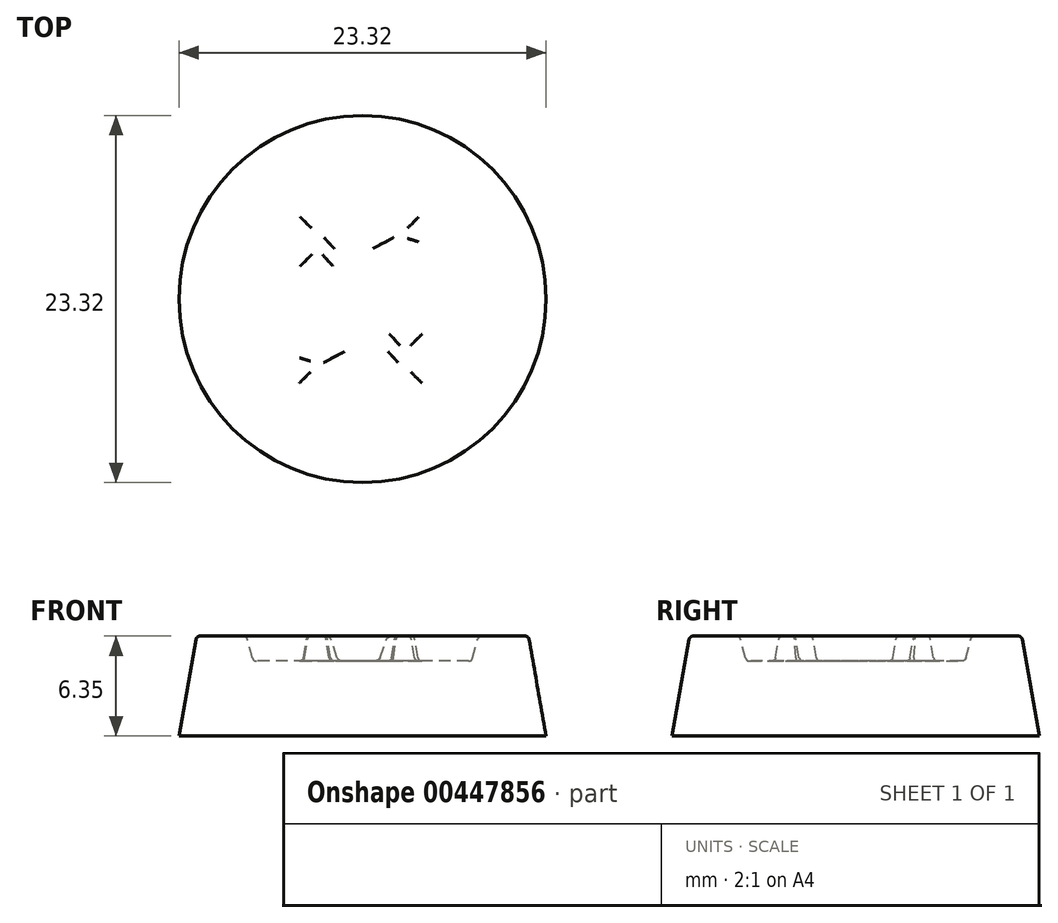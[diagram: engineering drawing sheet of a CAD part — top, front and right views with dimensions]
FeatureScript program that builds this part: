
annotation { "Feature Type Name" : "Feature", "Feature Type Description" : "" }
export const myFeature = defineFeature(function(context is Context, id is Id, definition is map)
    precondition{}
    {
        {
            var Q0;
            Q0=qCreatedBy(makeId("Top.planeOp"),FACE);
            var sketch = newSketch(context, id + "F0", { "sketchPlane" : qUnion([Q0])});
            skCircle(sketch, "E0", {"center": v(0, 0) * mm, "radius": 10.54 * mm});
            skSolve(sketch);
        }
        {
            var Q0;
            Q0=makeQuery(id+"F0.imprint","IMPRINT",FACE,{"disambiguationData":[TD([[makeQuery(id+"F0.imprint","IMPRINT",EDGE,{"derivedFrom":sQuery(id+"F0.wireOp",EDGE,"E0")}),1.0]])]});
            extrude(context, id + "F1", {"entities" : qUnion([Q0]), "oppositeDirection" : true, "depth" : 6.35 * mm, "hasDraft" : true, "draftAngle" : 10 * degree});
        }
        {
            var Q0;
            Q0=makeQuery(id+"F1.opExtrude","CAP_FACE",FACE,{"disambiguationData":[OSD([sQuery(id+"F0.wireOp",EDGE,"E0")])],"isStart":true});
            var sketch = newSketch(context, id + "F2", { "sketchPlane" : qUnion([Q0])});
            skCircle(sketch, "E1.0", {"center": v(0, 0) * mm, "radius": 7.37 * mm});
            skSolve(sketch);
        }
        {
            var Q0;
            Q0=makeQuery(id+"F2.imprint","IMPRINT",FACE,{"disambiguationData":[TD([[makeQuery(id+"F2.imprint","IMPRINT",EDGE,{"derivedFrom":sQuery(id+"F2.wireOp",EDGE,"E1.0")}),1.0]])]});
            extrude(context, id + "F3", {"entities" : qUnion([Q0]), "operationType" : NewBodyOperationType.REMOVE, "oppositeDirection" : true, "depth" : 1.59 * mm, "hasDraft" : true, "draftAngle" : 15 * degree, "draftPullDirection" : true});
        }
        {
            var Q0;
            Q0=makeQuery(id+"F1.opExtrude","CAP_FACE",FACE,{"disambiguationData":[OSD([sQuery(id+"F0.wireOp",EDGE,"E0")])],"isStart":true});
            var sketch = newSketch(context, id + "F4", { "sketchPlane" : qUnion([Q0])});
            skText(sketch, "E2", { "text": "Z", "fontName": "RobotoSlab-Regular.ttf"});
            skCircle(sketch, "E3.0", {"center": v(0, 0) * mm, "radius": 6.35 * mm, "construction": true});
            const initialGuessF4  = {"E2": [-0.00412, -0.00484, 1, 0, 0.00967]};
            skSetInitialGuess(sketch, initialGuessF4);
            skSolve(sketch);
        }
        {
            var Q0;
            Q0=makeQuery(id+"F4.imprint","IMPRINT",FACE,{"disambiguationData":[TD([[makeQuery(id+"F4.imprint","IMPRINT",EDGE,{"derivedFrom":sQuery(id+"F4.wireOp",EDGE,"E2.sketch_text.stroke-0")}),-1.0]])]});
            var Q1;
            Q1=makeQuery(id+"F3.boolean.opBoolean","COPY",FACE,{"derivedFrom":makeQuery(id+"F3.opExtrude","CAP_FACE",FACE,{"disambiguationData":[OSD([sQuery(id+"F2.wireOp",EDGE,"E1.0")])],"isStart":false})});
            extrude(context, id + "F5", {"entities" : qUnion([Q0]), "operationType" : NewBodyOperationType.ADD, "endBound" : BoundingType.UP_TO_SURFACE, "oppositeDirection" : true, "endBoundEntityFace" : qUnion([Q1]), "depth" : 25.4 * mm, "hasDraft" : true, "draftAngle" : 10 * degree});
        }
        {
            var Q0;
            Q0=makeQuery(id+"F5.opExtrude","CAP_FACE",FACE,{"disambiguationData":[OSD([sQuery(id+"F4.wireOp",EDGE,"E2.sketch_text.stroke-0"),sQuery(id+"F4.wireOp",EDGE,"E2.sketch_text.stroke-1"),sQuery(id+"F4.wireOp",EDGE,"E2.sketch_text.stroke-2"),sQuery(id+"F4.wireOp",EDGE,"E2.sketch_text.stroke-3"),sQuery(id+"F4.wireOp",EDGE,"E2.sketch_text.stroke-4"),sQuery(id+"F4.wireOp",EDGE,"E2.sketch_text.stroke-5"),sQuery(id+"F4.wireOp",EDGE,"E2.sketch_text.stroke-6"),sQuery(id+"F4.wireOp",EDGE,"E2.sketch_text.stroke-7"),sQuery(id+"F4.wireOp",EDGE,"E2.sketch_text.stroke-8"),sQuery(id+"F4.wireOp",EDGE,"E2.sketch_text.stroke-9"),sQuery(id+"F4.wireOp",EDGE,"E2.sketch_text.stroke-10"),sQuery(id+"F4.wireOp",EDGE,"E2.sketch_text.stroke-11"),sQuery(id+"F4.wireOp",EDGE,"E2.sketch_text.stroke-12"),sQuery(id+"F4.wireOp",EDGE,"E2.sketch_text.stroke-13"),sQuery(id+"F4.wireOp",EDGE,"E2.sketch_text.stroke-14"),sQuery(id+"F4.wireOp",EDGE,"E2.sketch_text.stroke-15"),sQuery(id+"F4.wireOp",EDGE,"E2.sketch_text.stroke-16"),sQuery(id+"F4.wireOp",EDGE,"E2.sketch_text.stroke-17"),sQuery(id+"F4.wireOp",EDGE,"E2.sketch_text.stroke-18"),sQuery(id+"F4.wireOp",EDGE,"E2.sketch_text.stroke-19"),sQuery(id+"F4.wireOp",EDGE,"E2.sketch_text.stroke-20"),sQuery(id+"F4.wireOp",EDGE,"E2.sketch_text.stroke-21"),sQuery(id+"F4.wireOp",EDGE,"E2.sketch_text.stroke-22"),sQuery(id+"F4.wireOp",EDGE,"E2.sketch_text.stroke-23"),sQuery(id+"F4.wireOp",EDGE,"E2.sketch_text.stroke-24"),sQuery(id+"F4.wireOp",EDGE,"E2.sketch_text.stroke-25")])],"isStart":true});
            var Q1;
            Q1=makeQuery(id+"F1.opExtrude","CAP_FACE",FACE,{"disambiguationData":[OSD([sQuery(id+"F0.wireOp",EDGE,"E0")])],"isStart":true});
            var Q2;
            Q2=makeQuery(id+"F3.boolean.opBoolean","COPY",FACE,{"derivedFrom":makeQuery(id+"F3.opExtrude","CAP_FACE",FACE,{"disambiguationData":[OSD([sQuery(id+"F2.wireOp",EDGE,"E1.0")])],"isStart":false})});
            fillet(context, id + "F6", {"entities" : qUnion([Q0, Q1, Q2]), "radius" : 0.25 * mm, "tangentPropagation" : true, "allowEdgeOverflow" : false});
        }
    });
